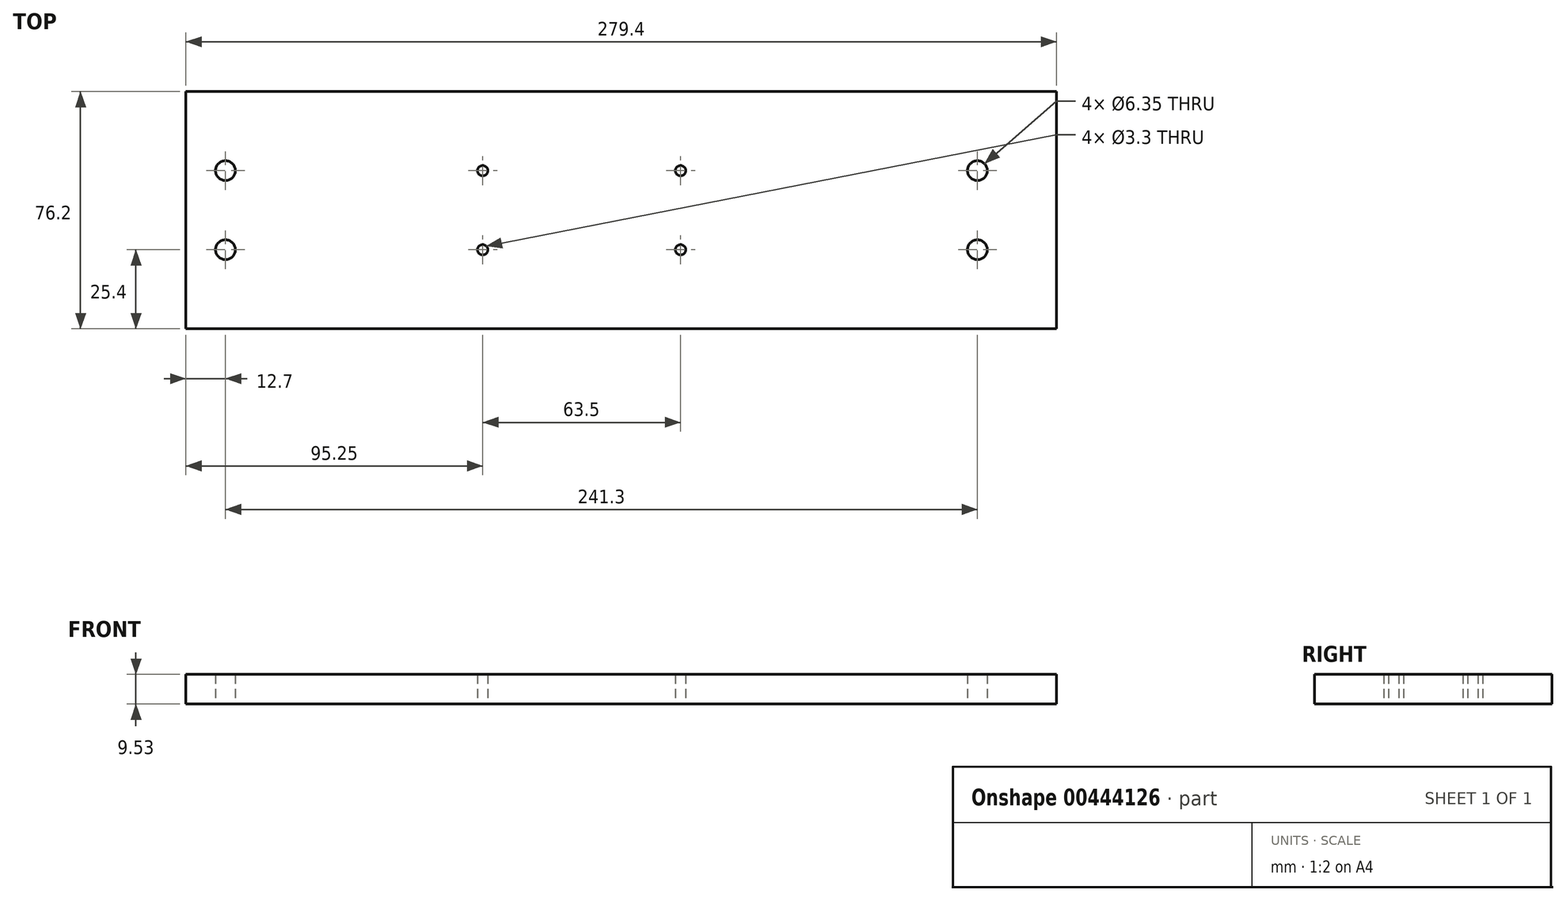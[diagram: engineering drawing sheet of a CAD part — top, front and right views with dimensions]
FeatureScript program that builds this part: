
annotation { "Feature Type Name" : "Feature", "Feature Type Description" : "" }
export const myFeature = defineFeature(function(context is Context, id is Id, definition is map)
    precondition{}
    {
        {
            var Q0;
            Q0=qCreatedBy(makeId("Top.planeOp"),FACE);
            var sketch = newSketch(context, id + "F0", { "sketchPlane" : qUnion([Q0])});
            skLineSegment(sketch, "E0.bottom", {"start": v(-139.7, 38.1) * mm, "end": v(139.7, 38.1) * mm});
            skLineSegment(sketch, "E0.top", {"start": v(-139.7, -38.1) * mm, "end": v(139.7, -38.1) * mm});
            skLineSegment(sketch, "E0.left", {"start": v(-139.7, 38.1) * mm, "end": v(-139.7, -38.1) * mm});
            skLineSegment(sketch, "E0.right", {"start": v(139.7, 38.1) * mm, "end": v(139.7, -38.1) * mm});
            skCircle(sketch, "E1", {"center": v(-127, 12.7) * mm, "radius": 3.18 * mm});
            skCircle(sketch, "E2", {"center": v(-127, -12.7) * mm, "radius": 3.18 * mm});
            skCircle(sketch, "E3", {"center": v(114.3, -12.7) * mm, "radius": 3.18 * mm});
            skCircle(sketch, "E4", {"center": v(114.3, 12.7) * mm, "radius": 3.18 * mm});
            skCircle(sketch, "E5", {"center": v(19.05, 12.7) * mm, "radius": 1.65 * mm});
            skCircle(sketch, "E6", {"center": v(19.05, -12.7) * mm, "radius": 1.65 * mm});
            skCircle(sketch, "E7", {"center": v(-44.45, -12.7) * mm, "radius": 1.65 * mm});
            skCircle(sketch, "E8", {"center": v(-44.45, 12.7) * mm, "radius": 1.65 * mm});
            skSolve(sketch);
        }
        {
            var Q0;
            Q0 = qSketchRegion(id + "F0", true);
            extrude(context, id + "F1", {"entities" : qUnion([Q0]), "depth" : 9.52 * mm});
        }
    });
